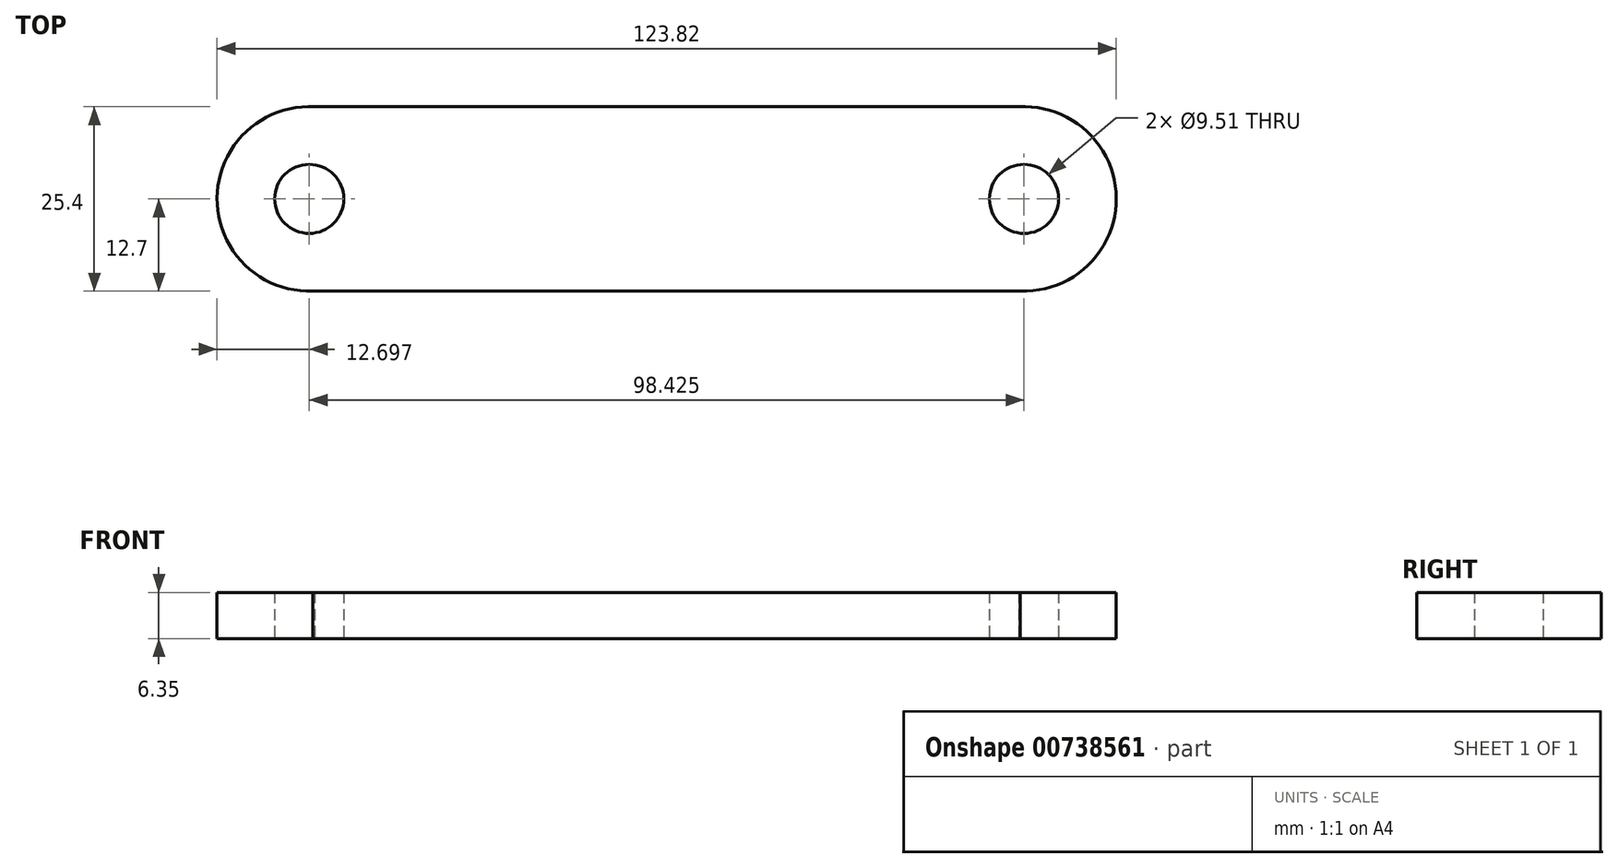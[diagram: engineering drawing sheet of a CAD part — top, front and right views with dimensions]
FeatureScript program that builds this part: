
annotation { "Feature Type Name" : "Feature", "Feature Type Description" : "" }
export const myFeature = defineFeature(function(context is Context, id is Id, definition is map)
    precondition{}
    {
        {
            var Q0;
            Q0=qCreatedBy(makeId("Top.planeOp"),FACE);
            var sketch = newSketch(context, id + "F0", { "sketchPlane" : qUnion([Q0])});
            skArc(sketch, "E0", {"start": v(-48.5, 12.68) * mm, "mid": v(-61.91, 0.1) * mm, "end": v(-48.72, -12.7) * mm});
            skLineSegment(sketch, "E1", {"start": v(-48.5, 12.68) * mm, "end": v(0, 12.68) * mm});
            skLineSegment(sketch, "E2", {"start": v(-48.72, -12.7) * mm, "end": v(0, -12.7) * mm});
            skCircle(sketch, "E3", {"center": v(-49.21, 0) * mm, "radius": 4.76 * mm});
            skLineSegment(sketch, "E4.MirrorCS", {"start": v(48.5, 12.68) * mm, "end": v(0, 12.68) * mm});
            skLineSegment(sketch, "E5.MirrorCS", {"start": v(48.72, -12.7) * mm, "end": v(0, -12.7) * mm});
            skArc(sketch, "E6.MirrorCS", {"start": v(48.5, 12.68) * mm, "mid": v(61.91, 0.1) * mm, "end": v(48.72, -12.7) * mm});
            skCircle(sketch, "E7.MirrorC", {"center": v(49.21, 0) * mm, "radius": 4.76 * mm});
            skSolve(sketch);
        }
        {
            var Q0;
            Q0 = qSketchRegion(id + "F0", true);
            extrude(context, id + "F1", {"entities" : qUnion([Q0]), "depth" : 6.35 * mm, "offsetDistance" : 25.4 * mm});
        }
    });
